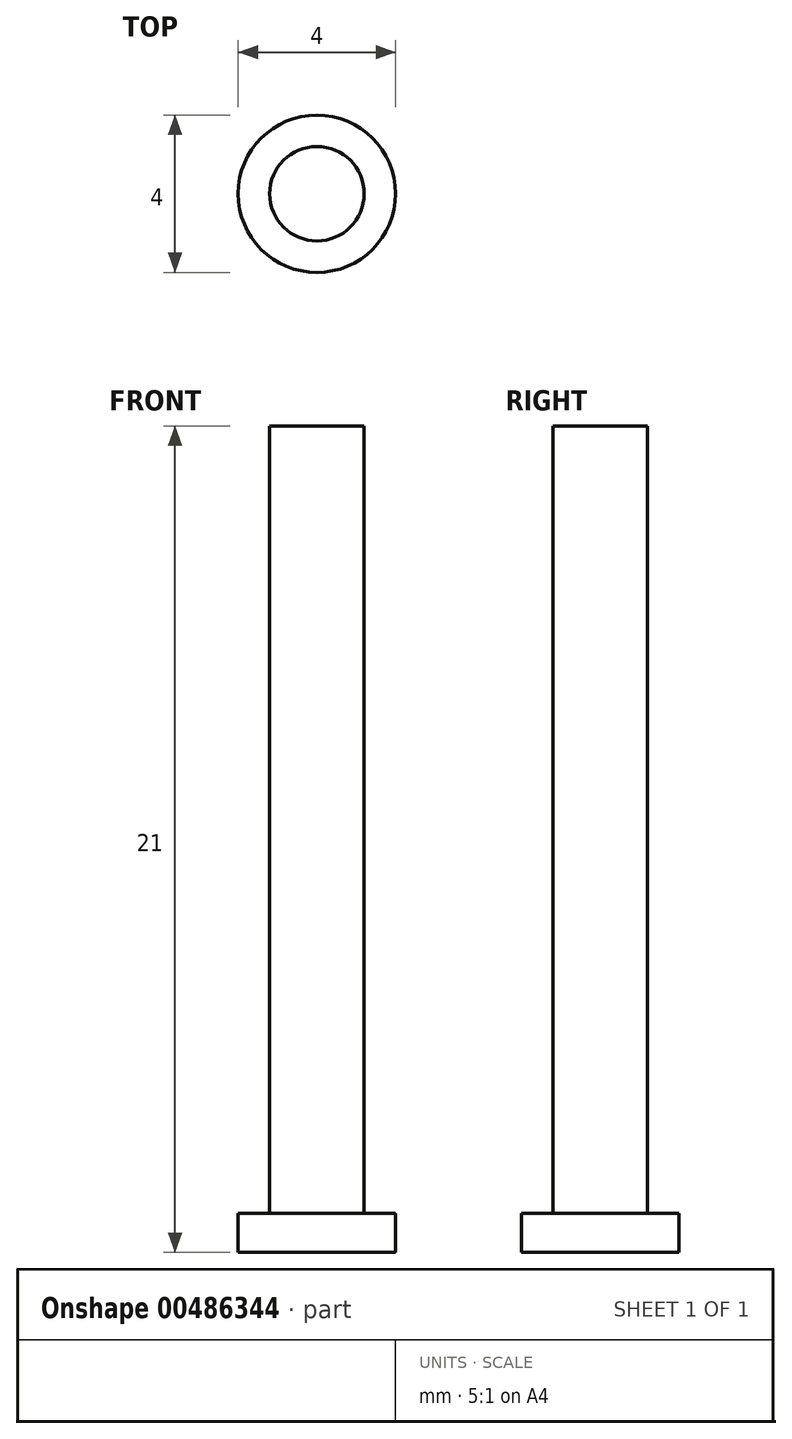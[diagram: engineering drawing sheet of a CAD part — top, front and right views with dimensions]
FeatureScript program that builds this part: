
annotation { "Feature Type Name" : "Feature", "Feature Type Description" : "" }
export const myFeature = defineFeature(function(context is Context, id is Id, definition is map)
    precondition{}
    {
        {
            var Q0;
            Q0=qCreatedBy(makeId("Front.planeOp"),FACE);
            var sketch = newSketch(context, id + "F0", { "sketchPlane" : qUnion([Q0])});
            skLineSegment(sketch, "E0", {"start": v(0, 0) * mm, "end": v(0, 20) * mm});
            skLineSegment(sketch, "E1", {"start": v(0, 20) * mm, "end": v(1.2, 20) * mm});
            skLineSegment(sketch, "E2", {"start": v(1.2, 20) * mm, "end": v(1.2, 0) * mm});
            skLineSegment(sketch, "E3", {"start": v(1.2, 0) * mm, "end": v(0, 0) * mm});
            skSolve(sketch);
        }
        {
            var Q0;
            Q0=makeQuery(id+"F0.imprint","IMPRINT",FACE,{"disambiguationData":[TD([[makeQuery(id+"F0.imprint","IMPRINT",EDGE,{"derivedFrom":sQuery(id+"F0.wireOp",EDGE,"E0")}),-1.0]])]});
            var Q1;
            Q1=sQuery(id+"F0.wireOp",EDGE,"E0");
            revolve(context, id + "F1", {"entities" : qUnion([Q0]), "axis" : qUnion([Q1]), "revolveType" : RevolveType.FULL});
        }
        {
            var Q0;
            Q0=qCreatedBy(makeId("Top.planeOp"),FACE);
            var sketch = newSketch(context, id + "F2", { "sketchPlane" : qUnion([Q0])});
            skCircle(sketch, "E4", {"center": v(0, 0) * mm, "radius": 2 * mm});
            skSolve(sketch);
        }
        {
            var Q0;
            Q0 = qSketchRegion(id + "F2", true);
            extrude(context, id + "F3", {"entities" : qUnion([Q0]), "operationType" : NewBodyOperationType.ADD, "oppositeDirection" : true, "depth" : 1 * mm});
        }
    });
